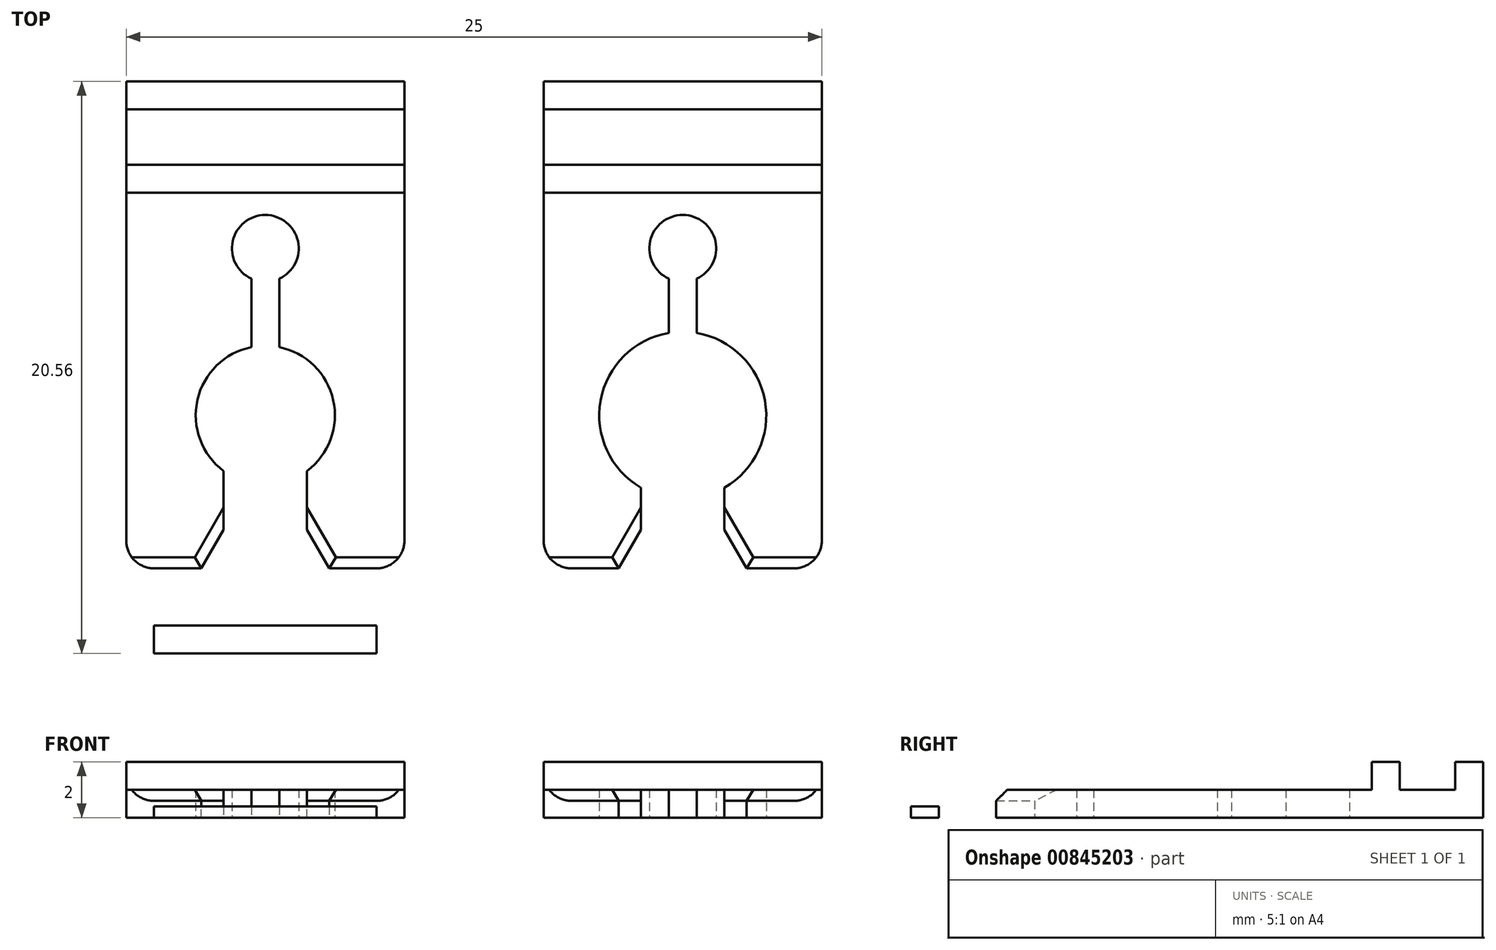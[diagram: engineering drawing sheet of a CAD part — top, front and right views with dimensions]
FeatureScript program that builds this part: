
annotation { "Feature Type Name" : "Feature", "Feature Type Description" : "" }
export const myFeature = defineFeature(function(context is Context, id is Id, definition is map)
    precondition{}
    {
        {
            var Q0;
            Q0=qCreatedBy(makeId("Top.planeOp"),FACE);
            var sketch = newSketch(context, id + "F0", { "sketchPlane" : qUnion([Q0])});
            skCircle(sketch, "E0", {"center": v(0, 0) * mm, "radius": 2.5 * mm});
            skCircle(sketch, "E1", {"center": v(0, 6) * mm, "radius": 1.2 * mm});
            skLineSegment(sketch, "E2.bottom", {"start": v(-5, 12) * mm, "end": v(5, 12) * mm});
            skLineSegment(sketch, "E2.top", {"start": v(-5, -5.5) * mm, "end": v(5, -5.5) * mm});
            skLineSegment(sketch, "E2.left", {"start": v(-5, 12) * mm, "end": v(-5, -5.5) * mm});
            skLineSegment(sketch, "E2.right", {"start": v(5, 12) * mm, "end": v(5, -5.5) * mm});
            skPoint(sketch, "E2.middle", {"position": v(0, 3.25) * mm});
            skLineSegment(sketch, "E3.bottom", {"start": v(-1.5, -5.5) * mm, "end": v(1.5, -5.5) * mm});
            skLineSegment(sketch, "E3.top", {"start": v(-1.5, -0.92) * mm, "end": v(1.5, -0.92) * mm});
            skLineSegment(sketch, "E3.left", {"start": v(-1.5, -5.5) * mm, "end": v(-1.5, -0.92) * mm});
            skLineSegment(sketch, "E3.right", {"start": v(1.5, -5.5) * mm, "end": v(1.5, -0.92) * mm});
            skPoint(sketch, "E3.middle", {"position": v(0, -3.2) * mm});
            skLineSegment(sketch, "E4.bottom", {"start": v(-0.5, 5.12) * mm, "end": v(0.5, 5.12) * mm});
            skLineSegment(sketch, "E4.top", {"start": v(-0.5, 2.08) * mm, "end": v(0.5, 2.08) * mm});
            skLineSegment(sketch, "E4.left", {"start": v(-0.5, 5.12) * mm, "end": v(-0.5, 2.08) * mm});
            skLineSegment(sketch, "E4.right", {"start": v(0.5, 5.12) * mm, "end": v(0.5, 2.08) * mm});
            skPoint(sketch, "E4.middle", {"position": v(0, 3.6) * mm});
            skLineSegment(sketch, "E5.top", {"start": v(-5, 11) * mm, "end": v(5, 11) * mm});
            skLineSegment(sketch, "E5.left", {"start": v(-5, 12) * mm, "end": v(-5, 11) * mm});
            skLineSegment(sketch, "E5.right", {"start": v(5, 12) * mm, "end": v(5, 11) * mm});
            skLineSegment(sketch, "E6.bottom", {"start": v(-5, 9) * mm, "end": v(5, 9) * mm});
            skLineSegment(sketch, "E6.top", {"start": v(-5, 8) * mm, "end": v(5, 8) * mm});
            skLineSegment(sketch, "E6.left", {"start": v(-5, 9) * mm, "end": v(-5, 8) * mm});
            skLineSegment(sketch, "E6.right", {"start": v(5, 9) * mm, "end": v(5, 8) * mm});
            skLineSegment(sketch, "E7.bottom", {"start": v(-4, -5.5) * mm, "end": v(-3, -5.5) * mm});
            skLineSegment(sketch, "E7.top", {"start": v(-4, -7.56) * mm, "end": v(-3, -7.56) * mm});
            skLineSegment(sketch, "E7.left", {"start": v(-4, -5.5) * mm, "end": v(-4, -7.56) * mm});
            skLineSegment(sketch, "E7.right", {"start": v(-3, -5.5) * mm, "end": v(-3, -7.56) * mm});
            skLineSegment(sketch, "E8.bottom", {"start": v(-4, -7.56) * mm, "end": v(4, -7.56) * mm});
            skLineSegment(sketch, "E8.top", {"start": v(-4, -8.56) * mm, "end": v(4, -8.56) * mm});
            skLineSegment(sketch, "E8.left", {"start": v(-4, -7.56) * mm, "end": v(-4, -8.56) * mm});
            skLineSegment(sketch, "E8.right", {"start": v(4, -7.56) * mm, "end": v(4, -8.56) * mm});
            skLineSegment(sketch, "E9.bottom", {"start": v(4, -7.56) * mm, "end": v(3, -7.56) * mm});
            skLineSegment(sketch, "E9.top", {"start": v(4, -5.5) * mm, "end": v(3, -5.5) * mm});
            skLineSegment(sketch, "E9.left", {"start": v(4, -7.56) * mm, "end": v(4, -5.5) * mm});
            skLineSegment(sketch, "E9.right", {"start": v(3, -7.56) * mm, "end": v(3, -5.5) * mm});
            skSolve(sketch);
        }
        {
            var Q0;
            Q0=makeQuery(id+"F0.imprint","IMPRINT",FACE,{"disambiguationData":[TD([[makeQuery(id+"F0.imprint","IMPRINT",EDGE,{"derivedFrom":sQuery(id+"F0.wireOp",EDGE,"E2.bottom")}),-1.0]])]});
            var Q1;
            {var subQ0=sQuery(id+"F0.wireOp",EDGE,"E5.top");Q1=makeQuery(id+"F0.imprint","IMPRINT",FACE,{"disambiguationData":[TD([[makeQuery(id+"F0.imprint","IMPRINT",EDGE,{"derivedFrom":subQ0}),-1.0]])]});}
            var Q2;
            Q2=makeQuery(id+"F0.imprint","IMPRINT",FACE,{"disambiguationData":[TD([[makeQuery(id+"F0.imprint","IMPRINT",EDGE,{"derivedFrom":sQuery(id+"F0.wireOp",EDGE,"E6.bottom")}),-1.0]])]});
            var Q3;
            {var subQ8=sQuery(id+"F0.wireOp",EDGE,"E6.top");Q3=makeQuery(id+"F0.imprint","IMPRINT",FACE,{"disambiguationData":[TD([[makeQuery(id+"F0.imprint","IMPRINT",EDGE,{"derivedFrom":subQ8}),-1.0]])]});}
            extrude(context, id + "F1", {"entities" : qUnion([Q0, Q1, Q2, Q3]), "depth" : 1 * mm, "offsetDistance" : 25 * mm});
        }
        {
            var Q0;
            Q0=makeQuery(id+"F0.imprint","IMPRINT",FACE,{"disambiguationData":[TD([[makeQuery(id+"F0.imprint","IMPRINT",EDGE,{"derivedFrom":sQuery(id+"F0.wireOp",EDGE,"E2.bottom")}),-1.0]])]});
            var Q1;
            Q1=makeQuery(id+"F0.imprint","IMPRINT",FACE,{"disambiguationData":[TD([[makeQuery(id+"F0.imprint","IMPRINT",EDGE,{"derivedFrom":sQuery(id+"F0.wireOp",EDGE,"E6.bottom")}),-1.0]])]});
            extrude(context, id + "F2", {"entities" : qUnion([Q0, Q1]), "operationType" : NewBodyOperationType.ADD, "depth" : 2 * mm, "offsetDistance" : 25 * mm});
        }
        {
            var Q0;
            Q0=makeQuery(id+"F1.opExtrude","SWEPT_EDGE",EDGE,{"disambiguationData":[OSD([sQuery(id+"F0.wireOp",EDGE,"E2.top"),sQuery(id+"F0.wireOp",EDGE,"E2.left")])]});
            var Q1;
            Q1=makeQuery(id+"F1.opExtrude","SWEPT_EDGE",EDGE,{"disambiguationData":[OSD([sQuery(id+"F0.wireOp",EDGE,"E2.top"),sQuery(id+"F0.wireOp",EDGE,"E2.right")])]});
            fillet(context, id + "F3", {"entities" : qUnion([Q0, Q1]), "radius" : 1 * mm, "tangentPropagation" : true, "allowEdgeOverflow" : false});
        }
        {
            var Q0;
            Q0=makeQuery(id+"F1.opExtrude","SWEPT_EDGE",EDGE,{"disambiguationData":[OSD([sQuery(id+"F0.wireOp",EDGE,"E2.top"),sQuery(id+"F0.wireOp",EDGE,"E3.bottom"),sQuery(id+"F0.wireOp",EDGE,"E3.left")])]});
            chamfer(context, id + "F4", {"entities" : qUnion([Q0]), "chamferType" : ChamferType.OFFSET_ANGLE, "width" : 0.8 * mm, "oppositeDirection" : true, "angle" : 60 * degree, "tangentPropagation" : true});
        }
        {
            var Q0;
            Q0=makeQuery(id+"F1.opExtrude","SWEPT_EDGE",EDGE,{"disambiguationData":[OSD([sQuery(id+"F0.wireOp",EDGE,"E2.top"),sQuery(id+"F0.wireOp",EDGE,"E3.bottom"),sQuery(id+"F0.wireOp",EDGE,"E3.right")])]});
            chamfer(context, id + "F5", {"entities" : qUnion([Q0]), "chamferType" : ChamferType.OFFSET_ANGLE, "width" : 0.8 * mm, "oppositeDirection" : false, "angle" : 60 * degree, "tangentPropagation" : true});
        }
        {
            var Q0;
            {var subQ0=sQuery(id+"F0.wireOp",EDGE,"E2.top");Q0=makeQuery(id+"F1.opExtrude","CAP_EDGE",EDGE,{"disambiguationData":[OSD([subQ0]),TDD([makeQuery(id+"F0.imprint","IMPRINT",EDGE,{"disambiguationData":[TD([[makeQuery(id+"F0.imprint","INTERSECT",VERTEX,{"derivedFrom":[subQ0,sQuery(id+"F0.wireOp",EDGE,"E2.left")]}),-1.0]])],"derivedFrom":subQ0})])],"isStart":false});}
            var Q1;
            {var subQ0=sQuery(id+"F0.wireOp",EDGE,"E2.top");Q1=makeQuery(id+"F1.opExtrude","CAP_EDGE",EDGE,{"disambiguationData":[OSD([subQ0]),TDD([makeQuery(id+"F0.imprint","IMPRINT",EDGE,{"disambiguationData":[TD([[makeQuery(id+"F0.imprint","INTERSECT",VERTEX,{"derivedFrom":[subQ0,sQuery(id+"F0.wireOp",EDGE,"E2.right")]}),1.0]])],"derivedFrom":subQ0})])],"isStart":false});}
            var Q2;
            {var subQ0=sQuery(id+"F0.wireOp",EDGE,"E3.right");var subQ1=sQuery(id+"F0.wireOp",EDGE,"E3.left");var subQ2=sQuery(id+"F0.wireOp",EDGE,"E6.right");var subQ3=sQuery(id+"F0.wireOp",EDGE,"E5.right");var subQ4=sQuery(id+"F0.wireOp",EDGE,"E2.right");var subQ5=sQuery(id+"F0.wireOp",EDGE,"E6.left");var subQ6=sQuery(id+"F0.wireOp",EDGE,"E5.left");var subQ7=sQuery(id+"F0.wireOp",EDGE,"E2.left");var subQ8=sQuery(id+"F0.wireOp",EDGE,"E2.top");var subQ9=sQuery(id+"F0.wireOp",EDGE,"E3.bottom");var subQ10=sQuery(id+"F0.wireOp",EDGE,"E4.left");var subQ11=sQuery(id+"F0.wireOp",EDGE,"E0");var subQ12=sQuery(id+"F0.wireOp",EDGE,"E4.right");var subQ13=sQuery(id+"F0.wireOp",EDGE,"E1");Q2=makeQuery(id+"F4.opChamfer","BLEND_EDGE",EDGE,{"blendedFrom":[makeQuery(id+"F1.opExtrude","SWEPT_EDGE",EDGE,{"disambiguationData":[OSD([subQ8,subQ9,subQ1])]}),makeQuery(id+"F2.boolean.opBoolean","SPLIT",FACE,{"disambiguationData":[TD([makeQuery(id+"F1.opExtrude","SWEPT_FACE",FACE,{"disambiguationData":[OSD([subQ13])]})])],"derivedFrom":makeQuery(id+"F1.opExtrude","CAP_FACE",FACE,{"disambiguationData":[OSD([subQ11,subQ13,subQ8,subQ7,subQ4,subQ1,subQ0,subQ10,subQ12,sQuery(id+"F0.wireOp",EDGE,"E2.bottom"),subQ6,subQ3,subQ5,subQ2])],"isStart":false})})],"blendedInto":[makeQuery(id+"F2.boolean.opBoolean","SPLIT",FACE,{"disambiguationData":[TD([makeQuery(id+"F1.opExtrude","SWEPT_FACE",FACE,{"disambiguationData":[OSD([subQ13])]})])],"derivedFrom":makeQuery(id+"F1.opExtrude","CAP_FACE",FACE,{"disambiguationData":[OSD([subQ11,subQ13,subQ8,subQ7,subQ4,subQ1,subQ0,subQ10,subQ12,sQuery(id+"F0.wireOp",EDGE,"E2.bottom"),subQ6,subQ3,subQ5,subQ2])],"isStart":false})})]});}
            var Q3;
            {var subQ0=sQuery(id+"F0.wireOp",EDGE,"E3.right");var subQ1=sQuery(id+"F0.wireOp",EDGE,"E3.left");var subQ2=sQuery(id+"F0.wireOp",EDGE,"E6.right");var subQ3=sQuery(id+"F0.wireOp",EDGE,"E5.right");var subQ4=sQuery(id+"F0.wireOp",EDGE,"E2.right");var subQ5=sQuery(id+"F0.wireOp",EDGE,"E6.left");var subQ6=sQuery(id+"F0.wireOp",EDGE,"E5.left");var subQ7=sQuery(id+"F0.wireOp",EDGE,"E2.left");var subQ8=sQuery(id+"F0.wireOp",EDGE,"E2.top");var subQ9=sQuery(id+"F0.wireOp",EDGE,"E3.bottom");var subQ10=sQuery(id+"F0.wireOp",EDGE,"E4.left");var subQ11=sQuery(id+"F0.wireOp",EDGE,"E0");var subQ12=sQuery(id+"F0.wireOp",EDGE,"E4.right");var subQ13=sQuery(id+"F0.wireOp",EDGE,"E1");Q3=makeQuery(id+"F5.opChamfer","BLEND_EDGE",EDGE,{"blendedFrom":[makeQuery(id+"F1.opExtrude","SWEPT_EDGE",EDGE,{"disambiguationData":[OSD([subQ8,subQ9,subQ0])]}),makeQuery(id+"F2.boolean.opBoolean","SPLIT",FACE,{"disambiguationData":[TD([makeQuery(id+"F1.opExtrude","SWEPT_FACE",FACE,{"disambiguationData":[OSD([subQ13])]})])],"derivedFrom":makeQuery(id+"F1.opExtrude","CAP_FACE",FACE,{"disambiguationData":[OSD([subQ11,subQ13,subQ8,subQ7,subQ4,subQ1,subQ0,subQ10,subQ12,sQuery(id+"F0.wireOp",EDGE,"E2.bottom"),subQ6,subQ3,subQ5,subQ2])],"isStart":false})})],"blendedInto":[makeQuery(id+"F2.boolean.opBoolean","SPLIT",FACE,{"disambiguationData":[TD([makeQuery(id+"F1.opExtrude","SWEPT_FACE",FACE,{"disambiguationData":[OSD([subQ13])]})])],"derivedFrom":makeQuery(id+"F1.opExtrude","CAP_FACE",FACE,{"disambiguationData":[OSD([subQ11,subQ13,subQ8,subQ7,subQ4,subQ1,subQ0,subQ10,subQ12,sQuery(id+"F0.wireOp",EDGE,"E2.bottom"),subQ6,subQ3,subQ5,subQ2])],"isStart":false})})]});}
            chamfer(context, id + "F6", {"entities" : qUnion([Q0, Q1, Q2, Q3]), "width" : 0.4 * mm});
        }
        {
            var Q0;
            Q0=makeQuery(id+"F0.imprint","IMPRINT",FACE,{"disambiguationData":[TD([[makeQuery(id+"F0.imprint","IMPRINT",EDGE,{"derivedFrom":sQuery(id+"F0.wireOp",EDGE,"E7.bottom")}),-1.0]])]});
            var Q1;
            Q1=makeQuery(id+"F0.imprint","IMPRINT",FACE,{"disambiguationData":[TD([[makeQuery(id+"F0.imprint","IMPRINT",EDGE,{"derivedFrom":sQuery(id+"F0.wireOp",EDGE,"E8.top")}),1.0]])]});
            var Q2;
            Q2=makeQuery(id+"F0.imprint","IMPRINT",FACE,{"disambiguationData":[TD([[makeQuery(id+"F0.imprint","IMPRINT",EDGE,{"derivedFrom":sQuery(id+"F0.wireOp",EDGE,"E9.bottom")}),-1.0]])]});
            extrude(context, id + "F7", {"entities" : qUnion([Q0, Q1, Q2]), "operationType" : NewBodyOperationType.ADD, "depth" : 0.4 * mm, "offsetDistance" : 25 * mm});
        }
        {
            var Q0;
            Q0=makeQuery(id+"F1.opExtrude","SWEPT_BODY",BODY,{"disambiguationData":[OSD([sQuery(id+"F0.wireOp",EDGE,"E0"),sQuery(id+"F0.wireOp",EDGE,"E1"),sQuery(id+"F0.wireOp",EDGE,"E2.top"),sQuery(id+"F0.wireOp",EDGE,"E2.left"),sQuery(id+"F0.wireOp",EDGE,"E2.right"),sQuery(id+"F0.wireOp",EDGE,"E3.left"),sQuery(id+"F0.wireOp",EDGE,"E3.right"),sQuery(id+"F0.wireOp",EDGE,"E4.left"),sQuery(id+"F0.wireOp",EDGE,"E4.right"),sQuery(id+"F0.wireOp",EDGE,"E2.bottom"),sQuery(id+"F0.wireOp",EDGE,"E5.left"),sQuery(id+"F0.wireOp",EDGE,"E5.right"),sQuery(id+"F0.wireOp",EDGE,"E6.left"),sQuery(id+"F0.wireOp",EDGE,"E6.right")])]});
            transform(context, id + "F8", {"entities" : qUnion([Q0]), "transformType" : TransformType.TRANSLATION_3D, "dx" : 15 * mm, "dy" : 0 * mm, "dz" : 0 * mm, "makeCopy" : true});
        }
        {
            var Q0;
            Q0=makeQuery(id+"F8.opPattern","COPY",FACE,{"derivedFrom":makeQuery(id+"F1.opExtrude","CAP_FACE",FACE,{"disambiguationData":[OSD([sQuery(id+"F0.wireOp",EDGE,"E0"),sQuery(id+"F0.wireOp",EDGE,"E1"),sQuery(id+"F0.wireOp",EDGE,"E2.top"),sQuery(id+"F0.wireOp",EDGE,"E2.left"),sQuery(id+"F0.wireOp",EDGE,"E2.right"),sQuery(id+"F0.wireOp",EDGE,"E3.left"),sQuery(id+"F0.wireOp",EDGE,"E3.right"),sQuery(id+"F0.wireOp",EDGE,"E4.left"),sQuery(id+"F0.wireOp",EDGE,"E4.right"),sQuery(id+"F0.wireOp",EDGE,"E2.bottom"),sQuery(id+"F0.wireOp",EDGE,"E5.left"),sQuery(id+"F0.wireOp",EDGE,"E5.right"),sQuery(id+"F0.wireOp",EDGE,"E6.left"),sQuery(id+"F0.wireOp",EDGE,"E6.right")])],"isStart":true}),"instanceName":"1"});
            var sketch = newSketch(context, id + "F9", { "sketchPlane" : qUnion([Q0])});
            skCircle(sketch, "E10", {"center": v(15, 0) * mm, "radius": 3 * mm});
            skSolve(sketch);
        }
        {
            var Q0;
            {var subQ4=sQuery(id+"F0.wireOp",EDGE,"E4.left");var subQ7=sQuery(id+"F0.wireOp",EDGE,"E0");var subQ8=makeQuery(id+"F8.opPattern","COPY",EDGE,{"derivedFrom":makeQuery(id+"F1.opExtrude","CAP_EDGE",EDGE,{"disambiguationData":[OSD([subQ7]),TDD([makeQuery(id+"F0.imprint","IMPRINT",EDGE,{"disambiguationData":[TD([[makeQuery(id+"F0.imprint","INTERSECT",VERTEX,{"derivedFrom":[subQ7,subQ4]}),-1.0]])],"derivedFrom":subQ7})])],"isStart":true}),"instanceName":"1"});Q0=makeQuery(id+"F9.imprint","IMPRINT",FACE,{"disambiguationData":[TD([[makeQuery(id+"F9.imprint","IMPRINT",EDGE,{"derivedFrom":subQ8}),1.0]])]});}
            var Q1;
            {var subQ4=sQuery(id+"F0.wireOp",EDGE,"E4.right");var subQ7=sQuery(id+"F0.wireOp",EDGE,"E0");var subQ8=makeQuery(id+"F8.opPattern","COPY",EDGE,{"derivedFrom":makeQuery(id+"F1.opExtrude","CAP_EDGE",EDGE,{"disambiguationData":[OSD([subQ7]),TDD([makeQuery(id+"F0.imprint","IMPRINT",EDGE,{"disambiguationData":[TD([[makeQuery(id+"F0.imprint","INTERSECT",VERTEX,{"derivedFrom":[subQ7,subQ4]}),1.0]])],"derivedFrom":subQ7})])],"isStart":true}),"instanceName":"1"});Q1=makeQuery(id+"F9.imprint","IMPRINT",FACE,{"disambiguationData":[TD([[makeQuery(id+"F9.imprint","IMPRINT",EDGE,{"derivedFrom":subQ8}),1.0]])]});}
            var Q2;
            Q2=sQuery(id+"F9.wireOp",EDGE,"E10");
            extrude(context, id + "F10", {"entities" : qUnion([Q0, Q1]), "operationType" : NewBodyOperationType.REMOVE, "surfaceEntities" : qUnion([Q2]), "oppositeDirection" : true, "depth" : 2 * mm, "offsetDistance" : 25 * mm});
        }
    });
